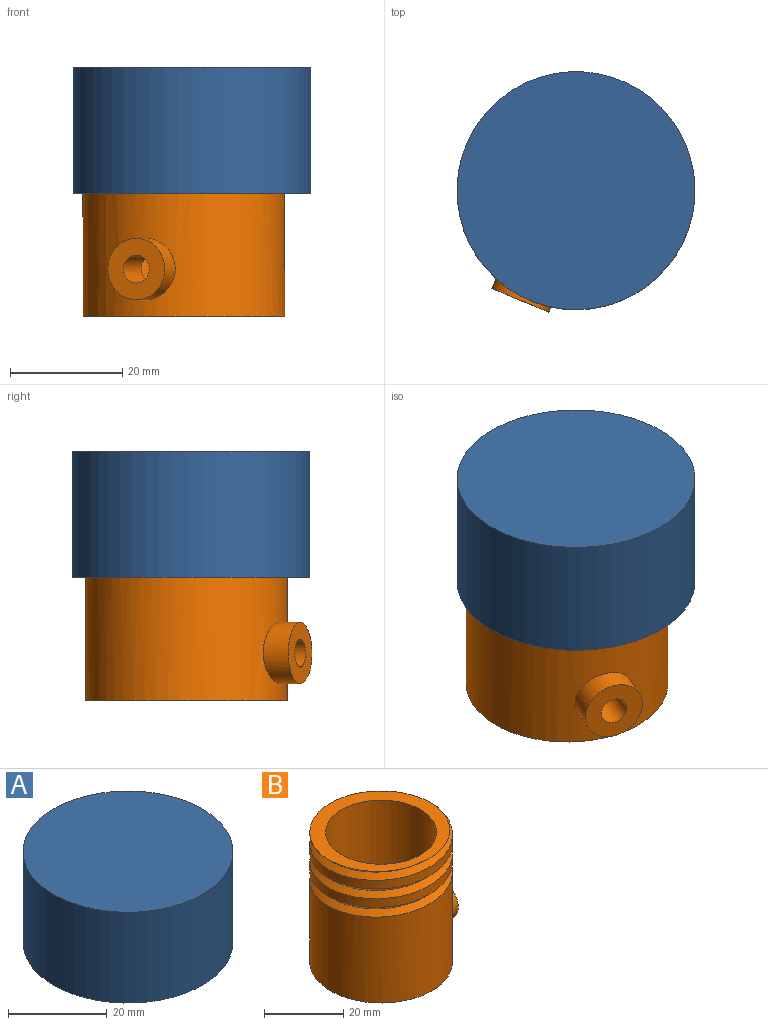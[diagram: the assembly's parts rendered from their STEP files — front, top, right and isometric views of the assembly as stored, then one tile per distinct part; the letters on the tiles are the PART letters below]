
ASSEMBLY  parts=2 mates=1
PART A: 14 faces, bbox 43.2x43.2x24 mm
  f0: plane 37.5x37.5mm, normal (0,0,1), area 58.1mm2, adj f3,f4,f10
  f1: bspline ~42.15x36.5mm, area 618.4mm2, adj f2,f3,f4,f5,f6,f7,f8
  f2: bspline ~42.15x36.5mm, area 565.5mm2, adj f1,f4,f5,f6,f7,f8
  f3: cylinder r=18.25mm len=36.5mm, axis (0,0,-1), area 81.2mm2, adj f0,f1,f4
  f4: cylinder r=18.25mm len=36.5mm, axis (0,0,-1), area 410.8mm2, adj f0,f1,f2,f3,f5,f8
  f5: cylinder r=18.25mm len=36.5mm, axis (0,0,-1), area 334.4mm2, adj f1,f2,f4,f6
  f6: cylinder r=18.25mm len=36.5mm, axis (0,0,-1), area 367.7mm2, adj f1,f2,f5,f7,f11
  f7: plane 37.13x18.97mm, normal (0,0,-1), area 37.2mm2, adj f1,f2,f6
  f8: plane 2.75x1.38mm, normal (0,1,0), area 1.9mm2, adj f1,f2,f4
  f9: plane 37.5x37.5mm, normal (0,0,-1), area 1104.5mm2, adj f10
  f10: cylinder r=18.75mm len=37.5mm, axis (0,0,-1), area 176.7mm2, adj f0,f9
  f11: plane 42.5x42.5mm, normal (0,0,-1), area 372.3mm2, adj f6,f13
  f12: plane 42.5x42.5mm, normal (0,0,1), area 1418.6mm2, adj f13
  f13: cylinder r=21.25mm len=42.5mm, axis (0,0,-1), area 3004.1mm2, adj f11,f12
PART B: 14 faces, bbox 40.8x42.3x42.8 mm
  f0: plane 36.63x35.39mm, normal (0,0,1), area 358.5mm2, adj f1,f4,f7,f8
  f1: cylinder r=14mm len=37mm, axis (0,0,1), area 3235mm2, adj f0,f10,f11
  f2: cylinder r=18mm len=36mm, axis (0,0,1), area 301.8mm2, adj f3,f5,f7,f8
  f3: cylinder r=18mm len=36mm, axis (0,0,1), area 301.7mm2, adj f2,f4,f7,f8
  f4: cylinder r=18mm len=35.66mm, axis (0,0,1), area 70.7mm2, adj f0,f3,f8
  f5: cylinder r=18mm len=36mm, axis (0,0,1), area 2825.4mm2, adj f2,f6,f7,f9,f12
  f6: plane 3x1.5mm, normal (0,1,0), area 2.2mm2, adj f5,f7,f8
  f7: bspline ~41.57x36mm, area 660.3mm2, adj f0,f2,f3,f5,f6,f8
  f8: bspline ~41.57x36mm, area 598.5mm2, adj f0,f2,f3,f4,f6,f7
  f9: plane 36x36mm, normal (0,0,-1), area 1017.9mm2, adj f5
  f10: plane 28x28mm, normal (0,0,1), area 615.8mm2, adj f1
  f11: cylinder r=2.5mm len=8mm, axis (1,0,0), area 125.7mm2, adj f1,f13
  f12: cylinder r=5.5mm len=11mm, axis (1,0,0), area 138.2mm2, adj f5,f13
  f13: plane 11x11mm, normal (1,0,0), area 75.4mm2, adj f11,f12
PLACE A rot(axis=(0,0,-1),22.6deg) t=(33.26,-62.2,-124.91)mm
PLACE B rot(axis=(0,0,-1),112.6deg) t=(31.79,-61.41,-138.67)mm
MATE cylindrical A.f3 <-> B.f0  axis (0,0,-1) through (33.26,-62.2,-117.16)mm
